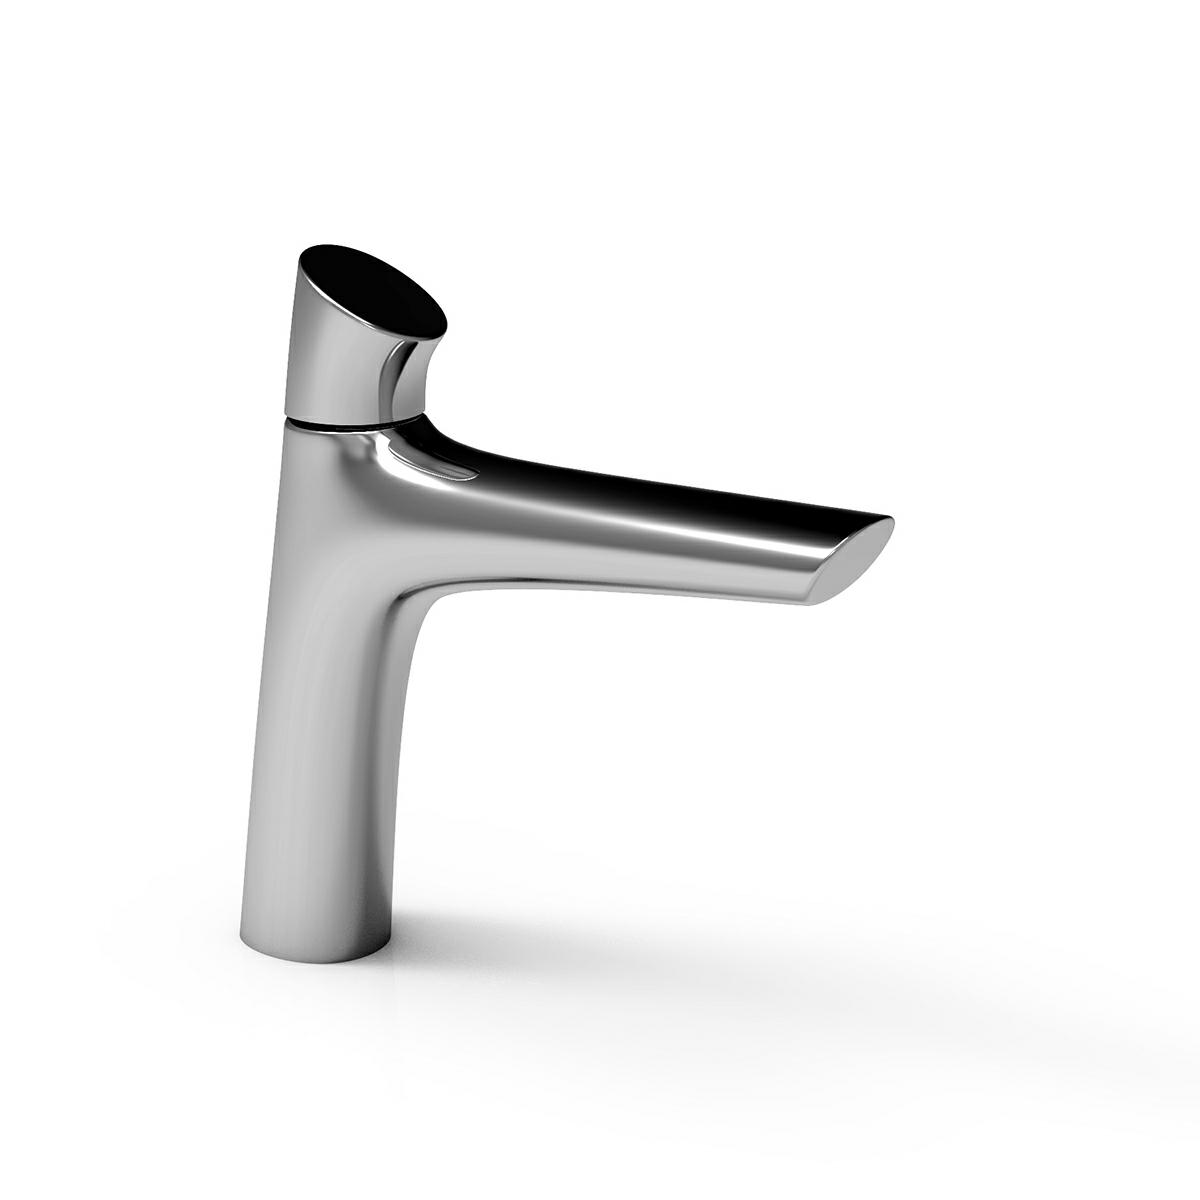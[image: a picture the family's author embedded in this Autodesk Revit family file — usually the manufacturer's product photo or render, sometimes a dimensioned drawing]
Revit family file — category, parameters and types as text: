
# Revit family: E-940
name_source: partatom
category: Plumbing Fixtures
units: mm (PartAtom-declared; Revit-internal decimal feet)

## family parameters
Always vertical = Yes
Cut with Voids When Loaded = No
OmniClass Number = 23.45.55.14
OmniClass Title = Single Faucets
Part Type = Normal
Room Calculation Point = Yes
Round Connector Dimension = Use Diameter
Shared = Yes
Work Plane-Based = Yes

## types (2) — shared parameters
Accesorios = Conectores ½ -14 NPSM
Cuerpo de Latón = Brass
Default Elevation = 1"
Garantía = El producto HELVEX está garantizado como libre de defectos en materiales y procesos de fabricación. El producto HELVEX está garantizado, en lo que se refiere a los acabados; por un periodo de 10 años en los acabados cromo y duravex, y por 2 años en acabados diferentes al cromo, a partir de la fecha de compra indicada en la factura
Instalación = Conexión ½ - 14 NPSM
Manufacturer = HELVEX S.A. de C.V.
Presión Máxima de Trabajo = 85.3 psi
Total Depth = 8"
Total Width = 2"
Type Comments = Monomando para lavabo con contra de push.

## per-type parameters (varying)
| type | Características del Producto | Description | Operación | Presión Mínima de Trabajo | Total Height | Type Image | URL |
| E-941 | Monomando para lavabo con contra de push. | Monomando para lavabo con contra de push. | El maneral tienen una rotación horizontal para la función de agua caliente y fría; y vertical para abrir y cerrar el flujo de agua. | 8.5 psi | 6" | <None> |  |
| E-940 | La suavidad del agua se materializa. Función y estética suaves que se adaptan a cualquier ambiente de baño.
Incluye contra de push. | Llave monomando de lavabo Alba | Levante el maneral para abrir el flujo y gire a la derecha para más fría o a la izquierda para más caliente. | 5.6 psi | 8" | E-940.jpg | https://www.helvex.com.mx |

note: column(s) folded — value = type name in every type: Model

## geometry (parser evidence)
native form markers: Sweep x2
no freeform markers — native parametric forms only
